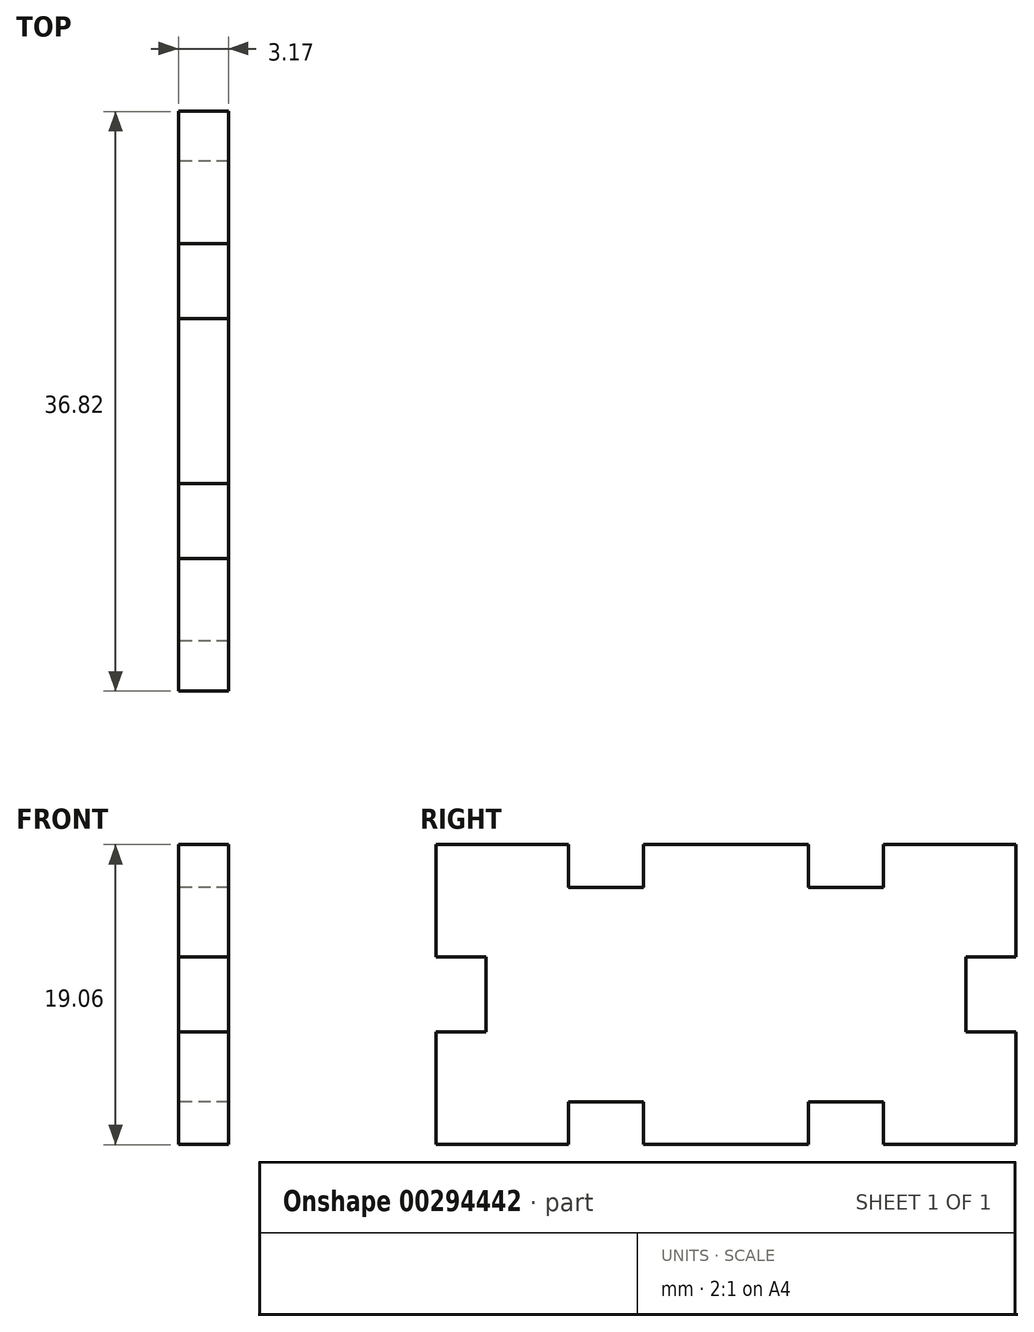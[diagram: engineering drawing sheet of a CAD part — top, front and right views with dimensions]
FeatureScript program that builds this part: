
annotation { "Feature Type Name" : "Feature", "Feature Type Description" : "" }
export const myFeature = defineFeature(function(context is Context, id is Id, definition is map)
    precondition{}
    {
        {
            var Q0;
            Q0=qCreatedBy(makeId("Right.planeOp"),FACE);
            var sketch = newSketch(context, id + "F0", { "sketchPlane" : qUnion([Q0])});
            skLineSegment(sketch, "E0.bottom", {"start": v(18.42, 9.52) * mm, "end": v(-18.42, 9.53) * mm});
            skLineSegment(sketch, "E0.top", {"start": v(18.42, -9.53) * mm, "end": v(-18.42, -9.52) * mm});
            skLineSegment(sketch, "E0.left", {"start": v(18.42, 9.53) * mm, "end": v(18.42, -9.52) * mm});
            skLineSegment(sketch, "E0.right", {"start": v(-18.41, 9.52) * mm, "end": v(-18.41, -9.52) * mm});
            skPoint(sketch, "E0.middle", {"position": v(0, 0) * mm});
            skLineSegment(sketch, "E1", {"start": v(-18.41, 0) * mm, "end": v(18.42, 0) * mm});
            skLineSegment(sketch, "E2", {"start": v(0, 9.53) * mm, "end": v(0, -9.53) * mm});
            skLineSegment(sketch, "E3", {"start": v(7.62, 9.53) * mm, "end": v(7.62, -9.53) * mm});
            skLineSegment(sketch, "E4", {"start": v(-7.62, 9.53) * mm, "end": v(-7.62, -9.52) * mm});
            skLineSegment(sketch, "E5.bottom", {"start": v(10, 12.23) * mm, "end": v(5.24, 12.23) * mm});
            skLineSegment(sketch, "E5.top", {"start": v(10, 6.82) * mm, "end": v(5.24, 6.82) * mm});
            skLineSegment(sketch, "E5.left", {"start": v(10, 12.23) * mm, "end": v(10, 6.82) * mm});
            skLineSegment(sketch, "E5.right", {"start": v(5.24, 12.23) * mm, "end": v(5.24, 6.82) * mm});
            skPoint(sketch, "E5.middle", {"position": v(7.62, 9.53) * mm});
            skLineSegment(sketch, "E6.bottom", {"start": v(-5.24, 12.23) * mm, "end": v(-10, 12.23) * mm});
            skLineSegment(sketch, "E6.top", {"start": v(-5.24, 6.82) * mm, "end": v(-10, 6.82) * mm});
            skLineSegment(sketch, "E6.left", {"start": v(-5.24, 12.23) * mm, "end": v(-5.24, 6.82) * mm});
            skLineSegment(sketch, "E6.right", {"start": v(-10, 12.23) * mm, "end": v(-10, 6.82) * mm});
            skPoint(sketch, "E6.middle", {"position": v(-7.62, 9.53) * mm});
            skLineSegment(sketch, "E7.bottom", {"start": v(-21.6, 2.38) * mm, "end": v(-15.24, 2.38) * mm});
            skLineSegment(sketch, "E7.top", {"start": v(-21.6, -2.38) * mm, "end": v(-15.24, -2.38) * mm});
            skLineSegment(sketch, "E7.left", {"start": v(-21.6, 2.38) * mm, "end": v(-21.6, -2.38) * mm});
            skLineSegment(sketch, "E7.right", {"start": v(-15.24, 2.38) * mm, "end": v(-15.24, -2.38) * mm});
            skPoint(sketch, "E7.middle", {"position": v(-18.42, 0) * mm});
            skLineSegment(sketch, "E8.bottom", {"start": v(21.59, 2.38) * mm, "end": v(15.24, 2.38) * mm});
            skLineSegment(sketch, "E8.top", {"start": v(21.59, -2.38) * mm, "end": v(15.24, -2.38) * mm});
            skLineSegment(sketch, "E8.left", {"start": v(21.59, 2.38) * mm, "end": v(21.59, -2.38) * mm});
            skLineSegment(sketch, "E8.right", {"start": v(15.24, 2.38) * mm, "end": v(15.24, -2.38) * mm});
            skPoint(sketch, "E8.middle", {"position": v(18.42, 0) * mm});
            skPoint(sketch, "E8.cornerSnap0", {"position": v(-18.42, 2.38) * mm});
            skLineSegment(sketch, "E9.MirrorCS", {"start": v(10, -12.23) * mm, "end": v(10, -6.82) * mm});
            skLineSegment(sketch, "E10.MirrorCS", {"start": v(5.24, -12.23) * mm, "end": v(5.24, -6.82) * mm});
            skLineSegment(sketch, "E11.MirrorCS", {"start": v(10, -6.82) * mm, "end": v(5.24, -6.82) * mm});
            skLineSegment(sketch, "E12.MirrorCS", {"start": v(-5.24, -6.82) * mm, "end": v(-10, -6.82) * mm});
            skLineSegment(sketch, "E13.MirrorCS", {"start": v(-5.24, -12.23) * mm, "end": v(-5.24, -6.82) * mm});
            skLineSegment(sketch, "E14.MirrorCS", {"start": v(-10, -12.23) * mm, "end": v(-10, -6.82) * mm});
            skLineSegment(sketch, "E15.MirrorCS", {"start": v(-5.24, -12.23) * mm, "end": v(-10, -12.23) * mm});
            skLineSegment(sketch, "E16.MirrorCS", {"start": v(10, -12.23) * mm, "end": v(5.24, -12.23) * mm});
            skSolve(sketch);
        }
        {
            var Q0;
            {var subQ5=sQuery(id+"F0.wireOp",EDGE,"E0.right");var subQ6=sQuery(id+"F0.wireOp",EDGE,"E0.bottom");var subQ7=makeQuery(id+"F0.imprint","INTERSECT",VERTEX,{"derivedFrom":[subQ6,subQ5]});Q0=makeQuery(id+"F0.imprint","IMPRINT",FACE,{"disambiguationData":[TD([[makeQuery(id+"F0.imprint","IMPRINT",EDGE,{"disambiguationData":[TD([[subQ7,1.0]])],"derivedFrom":subQ6}),1.0]])]});}
            var Q1;
            {var subQ5=sQuery(id+"F0.wireOp",EDGE,"E2");var subQ7=sQuery(id+"F0.wireOp",EDGE,"E0.bottom");var subQ8=makeQuery(id+"F0.imprint","INTERSECT",VERTEX,{"derivedFrom":[subQ7,subQ5]});Q1=makeQuery(id+"F0.imprint","IMPRINT",FACE,{"disambiguationData":[TD([[makeQuery(id+"F0.imprint","IMPRINT",EDGE,{"disambiguationData":[TD([[subQ8,-1.0]])],"derivedFrom":subQ7}),1.0]])]});}
            var Q2;
            {var subQ0=sQuery(id+"F0.wireOp",EDGE,"E2");var subQ1=sQuery(id+"F0.wireOp",EDGE,"E0.bottom");var subQ2=makeQuery(id+"F0.imprint","INTERSECT",VERTEX,{"derivedFrom":[subQ1,subQ0]});Q2=makeQuery(id+"F0.imprint","IMPRINT",FACE,{"disambiguationData":[TD([[makeQuery(id+"F0.imprint","IMPRINT",EDGE,{"disambiguationData":[TD([[subQ2,1.0]])],"derivedFrom":subQ1}),1.0]])]});}
            var Q3;
            {var subQ5=sQuery(id+"F0.wireOp",EDGE,"E0.left");var subQ6=sQuery(id+"F0.wireOp",EDGE,"E0.bottom");var subQ7=makeQuery(id+"F0.imprint","INTERSECT",VERTEX,{"derivedFrom":[subQ6,subQ5]});Q3=makeQuery(id+"F0.imprint","IMPRINT",FACE,{"disambiguationData":[TD([[makeQuery(id+"F0.imprint","IMPRINT",EDGE,{"disambiguationData":[TD([[subQ7,-1.0]])],"derivedFrom":subQ6}),1.0]])]});}
            var Q4;
            {var subQ9=sQuery(id+"F0.wireOp",EDGE,"E0.left");var subQ10=sQuery(id+"F0.wireOp",EDGE,"E0.top");var subQ11=makeQuery(id+"F0.imprint","INTERSECT",VERTEX,{"derivedFrom":[subQ10,subQ9]});Q4=makeQuery(id+"F0.imprint","IMPRINT",FACE,{"disambiguationData":[TD([[makeQuery(id+"F0.imprint","IMPRINT",EDGE,{"disambiguationData":[TD([[subQ11,-1.0]])],"derivedFrom":subQ10}),-1.0]])]});}
            var Q5;
            {var subQ5=sQuery(id+"F0.wireOp",EDGE,"E2");var subQ9=sQuery(id+"F0.wireOp",EDGE,"E0.top");var subQ11=makeQuery(id+"F0.imprint","INTERSECT",VERTEX,{"derivedFrom":[subQ9,subQ5]});Q5=makeQuery(id+"F0.imprint","IMPRINT",FACE,{"disambiguationData":[TD([[makeQuery(id+"F0.imprint","IMPRINT",EDGE,{"disambiguationData":[TD([[subQ11,1.0]])],"derivedFrom":subQ9}),-1.0]])]});}
            var Q6;
            {var subQ5=sQuery(id+"F0.wireOp",EDGE,"E2");var subQ6=sQuery(id+"F0.wireOp",EDGE,"E0.top");var subQ7=makeQuery(id+"F0.imprint","INTERSECT",VERTEX,{"derivedFrom":[subQ6,subQ5]});Q6=makeQuery(id+"F0.imprint","IMPRINT",FACE,{"disambiguationData":[TD([[makeQuery(id+"F0.imprint","IMPRINT",EDGE,{"disambiguationData":[TD([[subQ7,-1.0]])],"derivedFrom":subQ6}),-1.0]])]});}
            var Q7;
            {var subQ9=sQuery(id+"F0.wireOp",EDGE,"E0.right");var subQ10=sQuery(id+"F0.wireOp",EDGE,"E0.top");var subQ11=makeQuery(id+"F0.imprint","INTERSECT",VERTEX,{"derivedFrom":[subQ10,subQ9]});Q7=makeQuery(id+"F0.imprint","IMPRINT",FACE,{"disambiguationData":[TD([[makeQuery(id+"F0.imprint","IMPRINT",EDGE,{"disambiguationData":[TD([[subQ11,1.0]])],"derivedFrom":subQ10}),-1.0]])]});}
            extrude(context, id + "F1", {"entities" : qUnion([Q0, Q1, Q2, Q3, Q4, Q5, Q6, Q7]), "depth" : 3.17 * mm});
        }
    });
